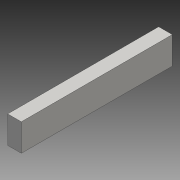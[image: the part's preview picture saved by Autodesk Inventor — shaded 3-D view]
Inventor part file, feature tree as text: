
AUTODESK INVENTOR PART (.ipt)
format: ipt  version: 2016 (Build 200138000, 138)  size: 69,120 bytes
history: native  units: mm
features: extrude x1, sketch x1
ambient origin geometry x8: Origin, YZ Plane, XZ Plane, XY Plane, X Axis, Y Axis, Z Axis, Center Point
bodies: 实体1 (feature_tree)
feature tree (2):
  extrude  "拉伸1"  Depth=20.0mm
  sketch  "草图1"  dims[d0=40.0mm d1=20.0mm d2=221.402mm d3=0.0mm]
